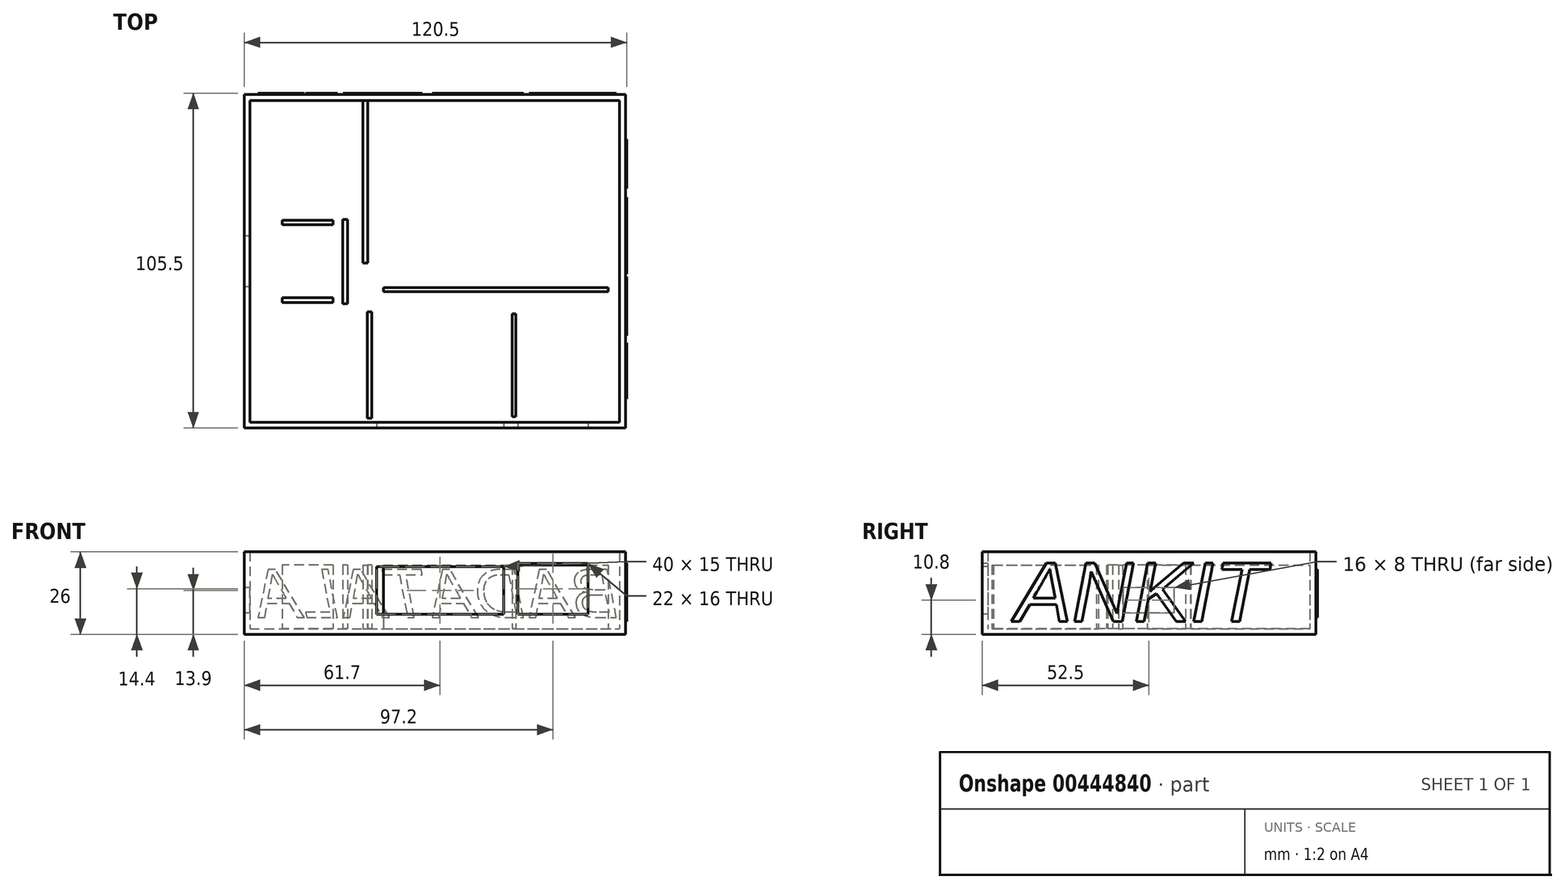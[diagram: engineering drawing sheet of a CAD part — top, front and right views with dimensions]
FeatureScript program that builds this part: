
annotation { "Feature Type Name" : "Feature", "Feature Type Description" : "" }
export const myFeature = defineFeature(function(context is Context, id is Id, definition is map)
    precondition{}
    {
        {
            var Q0;
            Q0=qCreatedBy(makeId("Top.planeOp"),FACE);
            var sketch = newSketch(context, id + "F0", { "sketchPlane" : qUnion([Q0])});
            skLineSegment(sketch, "E0.rect.bottom", {"start": v(-60, 52.5) * mm, "end": v(60, 52.5) * mm});
            skLineSegment(sketch, "E0.rect.top", {"start": v(-60, -52.5) * mm, "end": v(60, -52.5) * mm});
            skLineSegment(sketch, "E0.rect.left", {"start": v(-60, 52.5) * mm, "end": v(-60, -52.5) * mm});
            skLineSegment(sketch, "E0.rect.right", {"start": v(60, 52.5) * mm, "end": v(60, -52.5) * mm});
            skPoint(sketch, "E0.rect.middle", {"position": v(0, 0) * mm});
            skSolve(sketch);
        }
        {
            var Q0;
            Q0=makeQuery(id+"F0.imprint","IMPRINT",FACE,{"disambiguationData":[TD([[makeQuery(id+"F0.imprint","IMPRINT",EDGE,{"derivedFrom":sQuery(id+"F0.wireOp",EDGE,"E0.rect.bottom")}),-1.0]])]});
            extrude(context, id + "F1", {"entities" : qUnion([Q0]), "depth" : 26 * mm});
        }
        {
            var Q0;
            Q0=makeQuery(id+"F1.opExtrude","CAP_FACE",FACE,{"disambiguationData":[OSD([sQuery(id+"F0.wireOp",EDGE,"E0.rect.bottom"),sQuery(id+"F0.wireOp",EDGE,"E0.rect.top"),sQuery(id+"F0.wireOp",EDGE,"E0.rect.left"),sQuery(id+"F0.wireOp",EDGE,"E0.rect.right")])],"isStart":false});
            shell(context, id + "F2", {"entities" : qUnion([Q0]), "thickness" : 1.8 * mm});
        }
        {
            var Q0;
            Q0=makeQuery(id+"F1.opExtrude","SWEPT_FACE",FACE,{"disambiguationData":[OSD([sQuery(id+"F0.wireOp",EDGE,"E0.rect.top")])]});
            var sketch = newSketch(context, id + "F3", { "sketchPlane" : qUnion([Q0])});
            skLineSegment(sketch, "E1.bottom", {"start": v(26.2, 22.4) * mm, "end": v(48.2, 22.4) * mm});
            skLineSegment(sketch, "E1.top", {"start": v(26.2, 6.4) * mm, "end": v(48.2, 6.4) * mm});
            skLineSegment(sketch, "E1.left", {"start": v(26.2, 22.4) * mm, "end": v(26.2, 6.4) * mm});
            skLineSegment(sketch, "E1.right", {"start": v(48.2, 22.4) * mm, "end": v(48.2, 6.4) * mm});
            skLineSegment(sketch, "E2.bottom", {"start": v(-18.3, 21.4) * mm, "end": v(21.7, 21.4) * mm});
            skLineSegment(sketch, "E2.top", {"start": v(-18.3, 6.4) * mm, "end": v(21.7, 6.4) * mm});
            skLineSegment(sketch, "E2.left", {"start": v(-18.3, 21.4) * mm, "end": v(-18.3, 6.4) * mm});
            skLineSegment(sketch, "E2.right", {"start": v(21.7, 21.4) * mm, "end": v(21.7, 6.4) * mm});
            skSolve(sketch);
        }
        {
            var Q0;
            Q0=qSketchRegion(id+"F3",true);
            extrude(context, id + "F4", {"entities" : qUnion([Q0]), "operationType" : NewBodyOperationType.REMOVE, "endBound" : BoundingType.UP_TO_NEXT, "oppositeDirection" : true, "depth" : 25 * mm});
        }
        {
            var Q0;
            Q0=makeQuery(id+"F2.opShell","OFFSET_FACE",FACE,{"disambiguationData":[OSD([sQuery(id+"F0.wireOp",EDGE,"E0.rect.bottom"),sQuery(id+"F0.wireOp",EDGE,"E0.rect.top"),sQuery(id+"F0.wireOp",EDGE,"E0.rect.left"),sQuery(id+"F0.wireOp",EDGE,"E0.rect.right")])]});
            var sketch = newSketch(context, id + "F5", { "sketchPlane" : qUnion([Q0])});
            skLineSegment(sketch, "E3.bottom", {"start": v(-16.17, -9.5) * mm, "end": v(54.58, -9.5) * mm});
            skLineSegment(sketch, "E3.top", {"start": v(-16.17, -8.22) * mm, "end": v(54.58, -8.22) * mm});
            skLineSegment(sketch, "E3.left", {"start": v(-16.17, -9.5) * mm, "end": v(-16.17, -8.22) * mm});
            skLineSegment(sketch, "E3.right", {"start": v(54.58, -9.5) * mm, "end": v(54.58, -8.22) * mm});
            skLineSegment(sketch, "E4.bottom", {"start": v(25.48, -48.97) * mm, "end": v(24.42, -48.97) * mm});
            skLineSegment(sketch, "E4.top", {"start": v(25.48, -16.58) * mm, "end": v(24.42, -16.58) * mm});
            skLineSegment(sketch, "E4.left", {"start": v(25.48, -48.97) * mm, "end": v(25.48, -16.58) * mm});
            skLineSegment(sketch, "E4.right", {"start": v(24.42, -48.97) * mm, "end": v(24.42, -16.58) * mm});
            skLineSegment(sketch, "E5.bottom", {"start": v(-19.85, -49.46) * mm, "end": v(-21.24, -49.46) * mm});
            skLineSegment(sketch, "E5.top", {"start": v(-19.85, -15.88) * mm, "end": v(-21.24, -15.88) * mm});
            skLineSegment(sketch, "E5.left", {"start": v(-19.85, -49.46) * mm, "end": v(-19.85, -15.88) * mm});
            skLineSegment(sketch, "E5.right", {"start": v(-21.24, -49.46) * mm, "end": v(-21.24, -15.88) * mm});
            skSolve(sketch);
        }
        {
            var Q0;
            Q0=qSketchRegion(id+"F5",true);
            extrude(context, id + "F6", {"entities" : qUnion([Q0]), "operationType" : NewBodyOperationType.ADD, "depth" : 20 * mm});
        }
        {
            var Q0;
            Q0=makeQuery(id+"F2.opShell","OFFSET_FACE",FACE,{"disambiguationData":[OSD([sQuery(id+"F0.wireOp",EDGE,"E0.rect.bottom"),sQuery(id+"F0.wireOp",EDGE,"E0.rect.top"),sQuery(id+"F0.wireOp",EDGE,"E0.rect.left"),sQuery(id+"F0.wireOp",EDGE,"E0.rect.right")])]});
            var sketch = newSketch(context, id + "F7", { "sketchPlane" : qUnion([Q0])});
            skLineSegment(sketch, "E6.bottom", {"start": v(-32, 13) * mm, "end": v(-48, 13) * mm});
            skLineSegment(sketch, "E6.top", {"start": v(-32, 11.5) * mm, "end": v(-48, 11.5) * mm});
            skLineSegment(sketch, "E6.left", {"start": v(-32, 13) * mm, "end": v(-32, 11.5) * mm});
            skLineSegment(sketch, "E6.right", {"start": v(-48, 13) * mm, "end": v(-48, 11.5) * mm});
            skLineSegment(sketch, "E7.bottom", {"start": v(-27.5, 13.23) * mm, "end": v(-29, 13.23) * mm});
            skLineSegment(sketch, "E7.top", {"start": v(-27.5, -13.3) * mm, "end": v(-29, -13.3) * mm});
            skLineSegment(sketch, "E7.left", {"start": v(-27.5, 13.23) * mm, "end": v(-27.5, -13.3) * mm});
            skLineSegment(sketch, "E7.right", {"start": v(-29, 13.23) * mm, "end": v(-29, -13.3) * mm});
            skLineSegment(sketch, "E8.bottom", {"start": v(-32, -11.5) * mm, "end": v(-48, -11.5) * mm});
            skLineSegment(sketch, "E8.top", {"start": v(-32, -13) * mm, "end": v(-48, -13) * mm});
            skLineSegment(sketch, "E8.left", {"start": v(-32, -11.5) * mm, "end": v(-32, -13) * mm});
            skLineSegment(sketch, "E8.right", {"start": v(-48, -11.5) * mm, "end": v(-48, -13) * mm});
            skLineSegment(sketch, "E9.bottom", {"start": v(-17.01, -8.3) * mm, "end": v(46.8, -8.3) * mm});
            skLineSegment(sketch, "E10.bottom", {"start": v(-22.64, -0.52) * mm, "end": v(-21.06, -0.52) * mm});
            skLineSegment(sketch, "E10.top", {"start": v(-22.64, 50.7) * mm, "end": v(-21.06, 50.7) * mm});
            skLineSegment(sketch, "E10.left", {"start": v(-22.64, -0.52) * mm, "end": v(-22.64, 50.7) * mm});
            skLineSegment(sketch, "E10.right", {"start": v(-21.06, -0.52) * mm, "end": v(-21.06, 50.7) * mm});
            skSolve(sketch);
        }
        {
            var Q0;
            Q0=qSketchRegion(id+"F7",true);
            extrude(context, id + "F8", {"entities" : qUnion([Q0]), "operationType" : NewBodyOperationType.ADD, "depth" : 20 * mm});
        }
        {
            var Q0;
            Q0=makeQuery(id+"F1.opExtrude","SWEPT_FACE",FACE,{"disambiguationData":[OSD([sQuery(id+"F0.wireOp",EDGE,"E0.rect.left")])]});
            var sketch = newSketch(context, id + "F9", { "sketchPlane" : qUnion([Q0])});
            skLineSegment(sketch, "E11.rect.bottom", {"start": v(-8, 6.8) * mm, "end": v(8, 6.8) * mm});
            skLineSegment(sketch, "E11.rect.top", {"start": v(-8, 14.8) * mm, "end": v(8, 14.8) * mm});
            skLineSegment(sketch, "E11.rect.left", {"start": v(-8, 6.8) * mm, "end": v(-8, 14.8) * mm});
            skLineSegment(sketch, "E11.rect.right", {"start": v(8, 6.8) * mm, "end": v(8, 14.8) * mm});
            skPoint(sketch, "E11.rect.middle", {"position": v(0, 10.8) * mm});
            skSolve(sketch);
        }
        {
            var Q0;
            Q0=qSketchRegion(id+"F9",true);
            extrude(context, id + "F10", {"entities" : qUnion([Q0]), "operationType" : NewBodyOperationType.REMOVE, "endBound" : BoundingType.UP_TO_NEXT, "oppositeDirection" : true, "depth" : 25 * mm});
        }
        {
            var Q0;
            Q0=makeQuery(id+"F1.opExtrude","SWEPT_FACE",FACE,{"disambiguationData":[OSD([sQuery(id+"F0.wireOp",EDGE,"E0.rect.right")])]});
            var sketch = newSketch(context, id + "F11", { "sketchPlane" : qUnion([Q0])});
            skText(sketch, "E12", { "text": "ANKIT", "fontName": "Arimo-Italic.ttf"});
            const initialGuessF11  = {"E12": [-0.04205, 0.00404, 1, 0, 0.0193]};
            skSetInitialGuess(sketch, initialGuessF11);
            skSolve(sketch);
        }
        {
            var Q0;
            Q0=makeQuery(id+"F1.opExtrude","SWEPT_FACE",FACE,{"disambiguationData":[OSD([sQuery(id+"F0.wireOp",EDGE,"E0.rect.bottom")])]});
            var sketch = newSketch(context, id + "F12", { "sketchPlane" : qUnion([Q0])});
            skText(sketch, "E13", { "text": "BADATALA", "fontName": "Arimo-Italic.ttf"});
            const initialGuessF12  = {"E13": [-0.05784, 0.00536, 1, 0, 0.0158]};
            skSetInitialGuess(sketch, initialGuessF12);
            skSolve(sketch);
        }
        {
            var Q0;
            Q0 = qSketchRegion(id + "F11", true);
            extrude(context, id + "F13", {"entities" : qUnion([Q0]), "operationType" : NewBodyOperationType.ADD, "depth" : .5 * mm});
        }
        {
            var Q0;
            Q0 = qSketchRegion(id + "F12", true);
            extrude(context, id + "F14", {"entities" : qUnion([Q0]), "operationType" : NewBodyOperationType.ADD, "depth" : .5 * mm});
        }
    });
